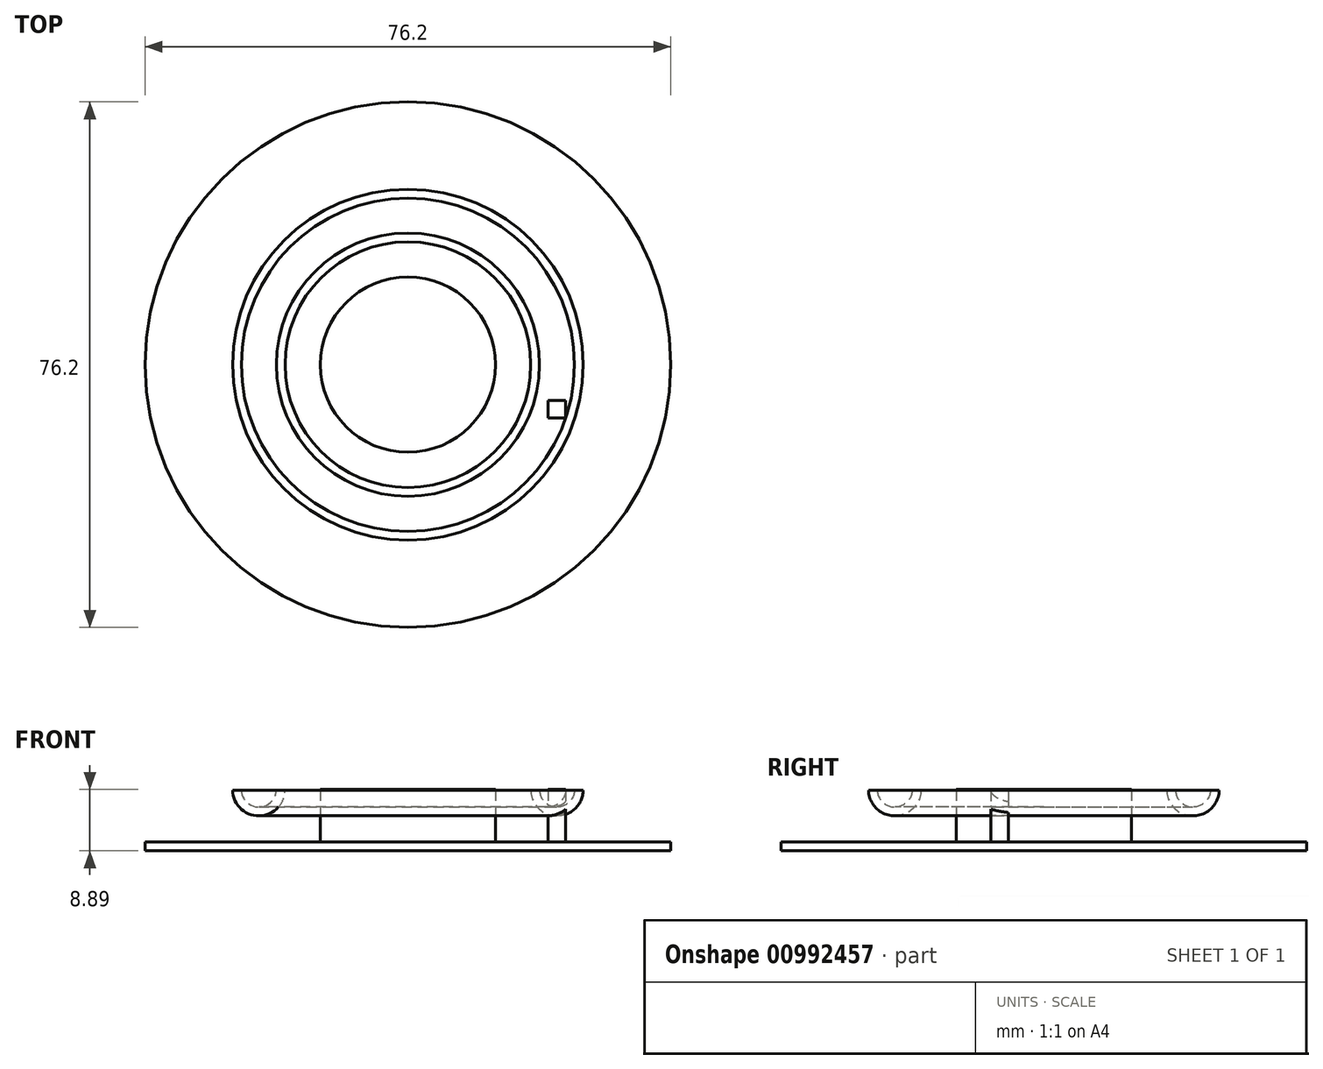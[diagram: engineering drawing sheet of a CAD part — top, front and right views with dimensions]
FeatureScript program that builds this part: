
annotation { "Feature Type Name" : "Feature", "Feature Type Description" : "" }
export const myFeature = defineFeature(function(context is Context, id is Id, definition is map)
    precondition{}
    {
        {
            var Q0;
            Q0=qCreatedBy(makeId("Top.planeOp"),FACE);
            var sketch = newSketch(context, id + "F0", { "sketchPlane" : qUnion([Q0])});
            skCircle(sketch, "E0", {"center": v(0, 0) * mm, "radius": 38.1 * mm});
            skPoint(sketch, "E1.right.start.orphan", {"position": v(25.8, 2) * mm});
            skPoint(sketch, "E1.left.end.orphan", {"position": v(23.26, 4.54) * mm});
            skPoint(sketch, "E1.left.start.orphan", {"position": v(23.26, 2) * mm});
            skSolve(sketch);
        }
        {
            var Q0;
            Q0=makeQuery(id+"F0.imprint","IMPRINT",FACE,{"disambiguationData":[TD([[makeQuery(id+"F0.imprint","IMPRINT",EDGE,{"derivedFrom":sQuery(id+"F0.wireOp",EDGE,"E0")}),1.0]])]});
            extrude(context, id + "F1", {"entities" : qUnion([Q0]), "depth" : 1.27 * mm, "offsetDistance" : 25.4 * mm});
        }
        {
            var Q0;
            Q0=makeQuery(id+"F1.opExtrude","CAP_FACE",FACE,{"disambiguationData":[OSD([sQuery(id+"F0.wireOp",EDGE,"E0")])],"isStart":false});
            var sketch = newSketch(context, id + "F2", { "sketchPlane" : qUnion([Q0])});
            skLineSegment(sketch, "E2.bottom", {"start": v(20.35, -5.17) * mm, "end": v(22.89, -5.17) * mm});
            skLineSegment(sketch, "E2.top", {"start": v(20.35, -7.7) * mm, "end": v(22.89, -7.7) * mm});
            skLineSegment(sketch, "E2.left", {"start": v(20.35, -5.17) * mm, "end": v(20.35, -7.7) * mm});
            skLineSegment(sketch, "E2.right", {"start": v(22.89, -5.17) * mm, "end": v(22.89, -7.7) * mm});
            skCircle(sketch, "E3", {"center": v(0, 0) * mm, "radius": 12.7 * mm});
            skSolve(sketch);
        }
        {
            var Q0;
            Q0=makeQuery(id+"F2.imprint","IMPRINT",FACE,{"disambiguationData":[TD([[makeQuery(id+"F2.imprint","IMPRINT",EDGE,{"derivedFrom":sQuery(id+"F2.wireOp",EDGE,"E2.bottom")}),-1.0]])]});
            var Q1;
            Q1=makeQuery(id+"F2.imprint","IMPRINT",FACE,{"disambiguationData":[TD([[makeQuery(id+"F2.imprint","IMPRINT",EDGE,{"derivedFrom":sQuery(id+"F2.wireOp",EDGE,"E3")}),1.0]])]});
            extrude(context, id + "F3", {"entities" : qUnion([Q0, Q1]), "operationType" : NewBodyOperationType.ADD, "depth" : 7.62 * mm, "offsetDistance" : 25.4 * mm});
        }
        {
            var Q0;
            Q0=qCreatedBy(makeId("Front.planeOp"),FACE);
            var sketch = newSketch(context, id + "F4", { "sketchPlane" : qUnion([Q0])});
            skArc(sketch, "E4", {"start": v(17.8, 8.8) * mm, "mid": v(21.62, 5.08) * mm, "end": v(25.43, 8.8) * mm});
            skLineSegment(sketch, "E5", {"start": v(17.8, 8.8) * mm, "end": v(19.08, 8.8) * mm});
            skArc(sketch, "E6", {"start": v(19.08, 8.8) * mm, "mid": v(21.62, 6.35) * mm, "end": v(24.15, 8.8) * mm});
            skLineSegment(sketch, "E7.trimOffspring", {"start": v(24.15, 8.8) * mm, "end": v(25.43, 8.8) * mm});
            skSolve(sketch);
        }
        {
            var Q0;
            Q0=makeQuery(id+"F4.imprint","IMPRINT",FACE,{"disambiguationData":[TD([[makeQuery(id+"F4.imprint","IMPRINT",EDGE,{"derivedFrom":sQuery(id+"F4.wireOp",EDGE,"E4")}),1.0]])]});
            var Q1;
            Q1=makeQuery(id+"F3.opExtrude","CAP_EDGE",EDGE,{"disambiguationData":[OSD([sQuery(id+"F2.wireOp",EDGE,"E3")])],"isStart":false});
            revolve(context, id + "F5", {"operationType" : NewBodyOperationType.ADD, "surfaceOperationType" : NewSurfaceOperationType.NEW, "entities" : qUnion([Q0]), "axis" : qUnion([Q1]), "revolveType" : RevolveType.FULL});
        }
    });
